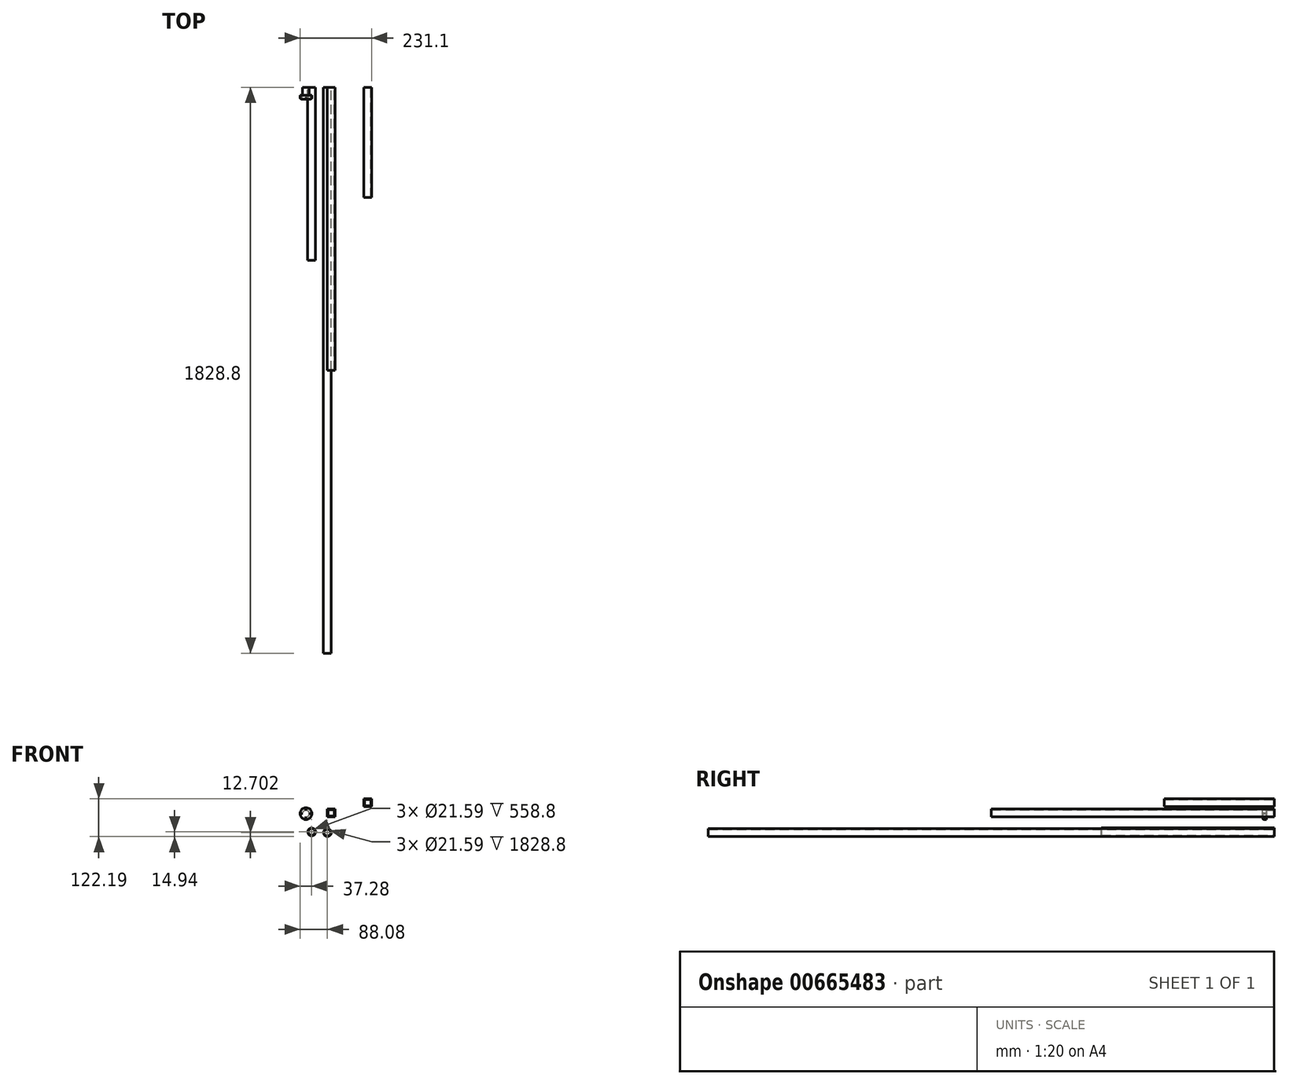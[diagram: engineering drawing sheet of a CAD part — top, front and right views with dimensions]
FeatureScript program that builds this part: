
annotation { "Feature Type Name" : "Feature", "Feature Type Description" : "" }
export const myFeature = defineFeature(function(context is Context, id is Id, definition is map)
    precondition{}
    {
        {
            var Q0;
            Q0=qCreatedBy(makeId("Front.planeOp"),FACE);
            var sketch = newSketch(context, id + "F0", { "sketchPlane" : qUnion([Q0])});
            skLineSegment(sketch, "E0.bottom", {"start": v(0, 74.59) * mm, "end": v(25.4, 74.59) * mm});
            skLineSegment(sketch, "E0.top", {"start": v(0, 49.19) * mm, "end": v(25.4, 49.19) * mm});
            skLineSegment(sketch, "E0.left", {"start": v(0, 74.59) * mm, "end": v(0, 49.19) * mm});
            skLineSegment(sketch, "E0.right", {"start": v(25.4, 74.59) * mm, "end": v(25.4, 49.19) * mm});
            skLineSegment(sketch, "E1.bottom", {"start": v(2.54, 72.05) * mm, "end": v(22.86, 72.05) * mm});
            skLineSegment(sketch, "E1.top", {"start": v(2.54, 51.73) * mm, "end": v(22.86, 51.73) * mm});
            skLineSegment(sketch, "E1.left", {"start": v(2.54, 72.05) * mm, "end": v(2.54, 51.73) * mm});
            skLineSegment(sketch, "E1.right", {"start": v(22.86, 72.05) * mm, "end": v(22.86, 51.73) * mm});
            skLineSegment(sketch, "E2.bottom", {"start": v(117.62, 107.25) * mm, "end": v(143.02, 107.25) * mm});
            skLineSegment(sketch, "E2.top", {"start": v(117.62, 81.85) * mm, "end": v(143.02, 81.85) * mm});
            skLineSegment(sketch, "E2.left", {"start": v(117.62, 107.25) * mm, "end": v(117.62, 81.85) * mm});
            skLineSegment(sketch, "E2.right", {"start": v(143.02, 107.25) * mm, "end": v(143.02, 81.85) * mm});
            skLineSegment(sketch, "E3.bottom", {"start": v(120.16, 104.7) * mm, "end": v(140.48, 104.7) * mm});
            skLineSegment(sketch, "E3.top", {"start": v(120.16, 84.39) * mm, "end": v(140.48, 84.39) * mm});
            skLineSegment(sketch, "E3.left", {"start": v(120.16, 104.7) * mm, "end": v(120.16, 84.39) * mm});
            skLineSegment(sketch, "E3.right", {"start": v(140.48, 104.7) * mm, "end": v(140.48, 84.39) * mm});
            skCircle(sketch, "E4", {"center": v(0, -2.24) * mm, "radius": 12.7 * mm});
            skCircle(sketch, "E5", {"center": v(0, -2.24) * mm, "radius": 10.8 * mm});
            skCircle(sketch, "E6", {"center": v(-50.8, 0) * mm, "radius": 12.7 * mm});
            skCircle(sketch, "E7", {"center": v(-50.8, 0) * mm, "radius": 10.8 * mm});
            skCircle(sketch, "E8", {"center": v(-69.03, 59) * mm, "radius": 10.8 * mm});
            skSolve(sketch);
        }
        {
            var Q0;
            Q0=makeQuery(id+"F0.imprint","IMPRINT",FACE,{"disambiguationData":[TD([[makeQuery(id+"F0.imprint","IMPRINT",EDGE,{"derivedFrom":sQuery(id+"F0.wireOp",EDGE,"E0.bottom")}),-1.0]])]});
            extrude(context, id + "F1", {"entities" : qUnion([Q0]), "depth" : 914.4 * mm, "offsetDistance" : 25.4 * mm});
        }
        {
            var Q0;
            Q0=makeQuery(id+"F0.imprint","IMPRINT",FACE,{"disambiguationData":[TD([[makeQuery(id+"F0.imprint","IMPRINT",EDGE,{"derivedFrom":sQuery(id+"F0.wireOp",EDGE,"E2.bottom")}),-1.0]])]});
            extrude(context, id + "F2", {"entities" : qUnion([Q0]), "depth" : 355.6 * mm, "offsetDistance" : 25.4 * mm});
        }
        {
            var Q0;
            Q0=makeQuery(id+"F0.imprint","IMPRINT",FACE,{"disambiguationData":[TD([[makeQuery(id+"F0.imprint","IMPRINT",EDGE,{"derivedFrom":sQuery(id+"F0.wireOp",EDGE,"E4")}),1.0]])]});
            extrude(context, id + "F3", {"entities" : qUnion([Q0]), "depth" : 1828.8 * mm, "offsetDistance" : 25.4 * mm});
        }
        {
            var Q0;
            Q0=makeQuery(id+"F0.imprint","IMPRINT",FACE,{"disambiguationData":[TD([[makeQuery(id+"F0.imprint","IMPRINT",EDGE,{"derivedFrom":sQuery(id+"F0.wireOp",EDGE,"E6")}),1.0]])]});
            extrude(context, id + "F4", {"entities" : qUnion([Q0]), "depth" : 558.8 * mm, "offsetDistance" : 25.4 * mm});
        }
        {
            var Q0;
            Q0=makeQuery(id+"F0.imprint","IMPRINT",FACE,{"disambiguationData":[TD([[makeQuery(id+"F0.imprint","IMPRINT",EDGE,{"derivedFrom":sQuery(id+"F0.wireOp",EDGE,"E8")}),1.0]])]});
            extrude(context, id + "F5", {"entities" : qUnion([Q0]), "depth" : 25.4 * mm, "offsetDistance" : 25.4 * mm});
        }
        {
            var Q0;
            Q0=makeQuery(id+"F5.opExtrude","CAP_FACE",FACE,{"disambiguationData":[OSD([sQuery(id+"F0.wireOp",EDGE,"E8")])],"isStart":false});
            var sketch = newSketch(context, id + "F6", { "sketchPlane" : qUnion([Q0])});
            skCircle(sketch, "E9", {"center": v(-69.03, 59) * mm, "radius": 19.05 * mm});
            skSolve(sketch);
        }
        {
            var Q0;
            Q0=makeQuery(id+"F6.imprint","IMPRINT",FACE,{"disambiguationData":[TD([[makeQuery(id+"F6.imprint","IMPRINT",EDGE,{"derivedFrom":sQuery(id+"F6.wireOp",EDGE,"E9")}),1.0]])]});
            var Q1;
            Q1=makeQuery(id+"F6.imprint","IMPRINT",FACE,{"disambiguationData":[TD([[makeQuery(id+"F6.imprint","IMPRINT",EDGE,{"derivedFrom":makeQuery(id+"F5.opExtrude","CAP_EDGE",EDGE,{"disambiguationData":[OSD([sQuery(id+"F0.wireOp",EDGE,"E8")])],"isStart":false})}),1.0]])]});
            extrude(context, id + "F7", {"entities" : qUnion([Q0, Q1]), "operationType" : NewBodyOperationType.ADD, "depth" : 12.7 * mm, "offsetDistance" : 25.4 * mm});
        }
        {
            var Q0;
            Q0=makeQuery(id+"F7.opExtrude","CAP_FACE",FACE,{"disambiguationData":[OSD([sQuery(id+"F6.wireOp",EDGE,"E9")])],"isStart":false});
            var sketch = newSketch(context, id + "F8", { "sketchPlane" : qUnion([Q0])});
            skCircle(sketch, "E10", {"center": v(-84.27, 59) * mm, "radius": 1.59 * mm});
            skCircle(sketch, "E11", {"center": v(-53.79, 59) * mm, "radius": 1.59 * mm});
            skCircle(sketch, "E12", {"center": v(-69.03, 74.25) * mm, "radius": 1.59 * mm});
            skCircle(sketch, "E13", {"center": v(-69.09, 43.77) * mm, "radius": 1.59 * mm});
            skSolve(sketch);
        }
        {
            var Q0;
            Q0=makeQuery(id+"F8.imprint","IMPRINT",FACE,{"disambiguationData":[TD([[makeQuery(id+"F8.imprint","IMPRINT",EDGE,{"derivedFrom":sQuery(id+"F8.wireOp",EDGE,"E10")}),1.0]])]});
            var Q1;
            Q1=makeQuery(id+"F8.imprint","IMPRINT",FACE,{"disambiguationData":[TD([[makeQuery(id+"F8.imprint","IMPRINT",EDGE,{"derivedFrom":sQuery(id+"F8.wireOp",EDGE,"E12")}),1.0]])]});
            var Q2;
            Q2=makeQuery(id+"F8.imprint","IMPRINT",FACE,{"disambiguationData":[TD([[makeQuery(id+"F8.imprint","IMPRINT",EDGE,{"derivedFrom":sQuery(id+"F8.wireOp",EDGE,"E11")}),1.0]])]});
            var Q3;
            Q3=makeQuery(id+"F8.imprint","IMPRINT",FACE,{"disambiguationData":[TD([[makeQuery(id+"F8.imprint","IMPRINT",EDGE,{"derivedFrom":sQuery(id+"F8.wireOp",EDGE,"E13")}),1.0]])]});
            extrude(context, id + "F9", {"entities" : qUnion([Q0, Q1, Q2, Q3]), "operationType" : NewBodyOperationType.REMOVE, "oppositeDirection" : true, "depth" : 25.4 * mm, "offsetDistance" : 25.4 * mm});
        }
        {
            var Q0;
            Q0=makeQuery(id+"F7.opExtrude","CAP_EDGE",EDGE,{"disambiguationData":[OSD([sQuery(id+"F6.wireOp",EDGE,"E9")])],"isStart":false});
            fillet(context, id + "F10", {"entities" : qUnion([Q0]), "radius" : 5.08 * mm, "tangentPropagation" : true, "allowEdgeOverflow" : false});
        }
        {
            var Q0;
            Q0=makeQuery(id+"F10.opFillet","BLEND_EDGE",EDGE,{"blendedFrom":[makeQuery(id+"F7.opExtrude","CAP_EDGE",EDGE,{"disambiguationData":[OSD([sQuery(id+"F6.wireOp",EDGE,"E9")])],"isStart":false}),makeQuery(id+"F9.boolean.opBoolean","COPY",FACE,{"derivedFrom":makeQuery(id+"F9.opExtrude","SWEPT_FACE",FACE,{"disambiguationData":[OSD([sQuery(id+"F8.wireOp",EDGE,"E13")])]})})],"blendedInto":[makeQuery(id+"F9.boolean.opBoolean","COPY",FACE,{"derivedFrom":makeQuery(id+"F9.opExtrude","SWEPT_FACE",FACE,{"disambiguationData":[OSD([sQuery(id+"F8.wireOp",EDGE,"E13")])]})})]});
            var Q1;
            Q1=makeQuery(id+"F9.boolean.opBoolean","COPY",EDGE,{"derivedFrom":makeQuery(id+"F9.opExtrude","CAP_EDGE",EDGE,{"disambiguationData":[OSD([sQuery(id+"F8.wireOp",EDGE,"E13")])],"isStart":true})});
            var Q2;
            Q2=makeQuery(id+"F10.opFillet","BLEND_EDGE",EDGE,{"blendedFrom":[makeQuery(id+"F7.opExtrude","CAP_EDGE",EDGE,{"disambiguationData":[OSD([sQuery(id+"F6.wireOp",EDGE,"E9")])],"isStart":false}),makeQuery(id+"F9.boolean.opBoolean","COPY",FACE,{"derivedFrom":makeQuery(id+"F9.opExtrude","SWEPT_FACE",FACE,{"disambiguationData":[OSD([sQuery(id+"F8.wireOp",EDGE,"E11")])]})})],"blendedInto":[makeQuery(id+"F9.boolean.opBoolean","COPY",FACE,{"derivedFrom":makeQuery(id+"F9.opExtrude","SWEPT_FACE",FACE,{"disambiguationData":[OSD([sQuery(id+"F8.wireOp",EDGE,"E11")])]})})]});
            var Q3;
            Q3=makeQuery(id+"F9.boolean.opBoolean","COPY",EDGE,{"derivedFrom":makeQuery(id+"F9.opExtrude","CAP_EDGE",EDGE,{"disambiguationData":[OSD([sQuery(id+"F8.wireOp",EDGE,"E11")])],"isStart":true})});
            var Q4;
            Q4=makeQuery(id+"F10.opFillet","BLEND_EDGE",EDGE,{"blendedFrom":[makeQuery(id+"F7.opExtrude","CAP_EDGE",EDGE,{"disambiguationData":[OSD([sQuery(id+"F6.wireOp",EDGE,"E9")])],"isStart":false}),makeQuery(id+"F9.boolean.opBoolean","COPY",FACE,{"derivedFrom":makeQuery(id+"F9.opExtrude","SWEPT_FACE",FACE,{"disambiguationData":[OSD([sQuery(id+"F8.wireOp",EDGE,"E10")])]})})],"blendedInto":[makeQuery(id+"F9.boolean.opBoolean","COPY",FACE,{"derivedFrom":makeQuery(id+"F9.opExtrude","SWEPT_FACE",FACE,{"disambiguationData":[OSD([sQuery(id+"F8.wireOp",EDGE,"E10")])]})})]});
            var Q5;
            Q5=makeQuery(id+"F9.boolean.opBoolean","COPY",EDGE,{"derivedFrom":makeQuery(id+"F9.opExtrude","CAP_EDGE",EDGE,{"disambiguationData":[OSD([sQuery(id+"F8.wireOp",EDGE,"E10")])],"isStart":true})});
            var Q6;
            Q6=makeQuery(id+"F10.opFillet","BLEND_EDGE",EDGE,{"blendedFrom":[makeQuery(id+"F7.opExtrude","CAP_EDGE",EDGE,{"disambiguationData":[OSD([sQuery(id+"F6.wireOp",EDGE,"E9")])],"isStart":false}),makeQuery(id+"F9.boolean.opBoolean","COPY",FACE,{"derivedFrom":makeQuery(id+"F9.opExtrude","SWEPT_FACE",FACE,{"disambiguationData":[OSD([sQuery(id+"F8.wireOp",EDGE,"E12")])]})})],"blendedInto":[makeQuery(id+"F9.boolean.opBoolean","COPY",FACE,{"derivedFrom":makeQuery(id+"F9.opExtrude","SWEPT_FACE",FACE,{"disambiguationData":[OSD([sQuery(id+"F8.wireOp",EDGE,"E12")])]})})]});
            var Q7;
            Q7=makeQuery(id+"F9.boolean.opBoolean","COPY",EDGE,{"derivedFrom":makeQuery(id+"F9.opExtrude","CAP_EDGE",EDGE,{"disambiguationData":[OSD([sQuery(id+"F8.wireOp",EDGE,"E12")])],"isStart":true})});
            fillet(context, id + "F11", {"entities" : qUnion([Q0, Q1, Q2, Q3, Q4, Q5, Q6, Q7]), "radius" : 0.89 * mm, "tangentPropagation" : true, "allowEdgeOverflow" : false});
        }
    });
